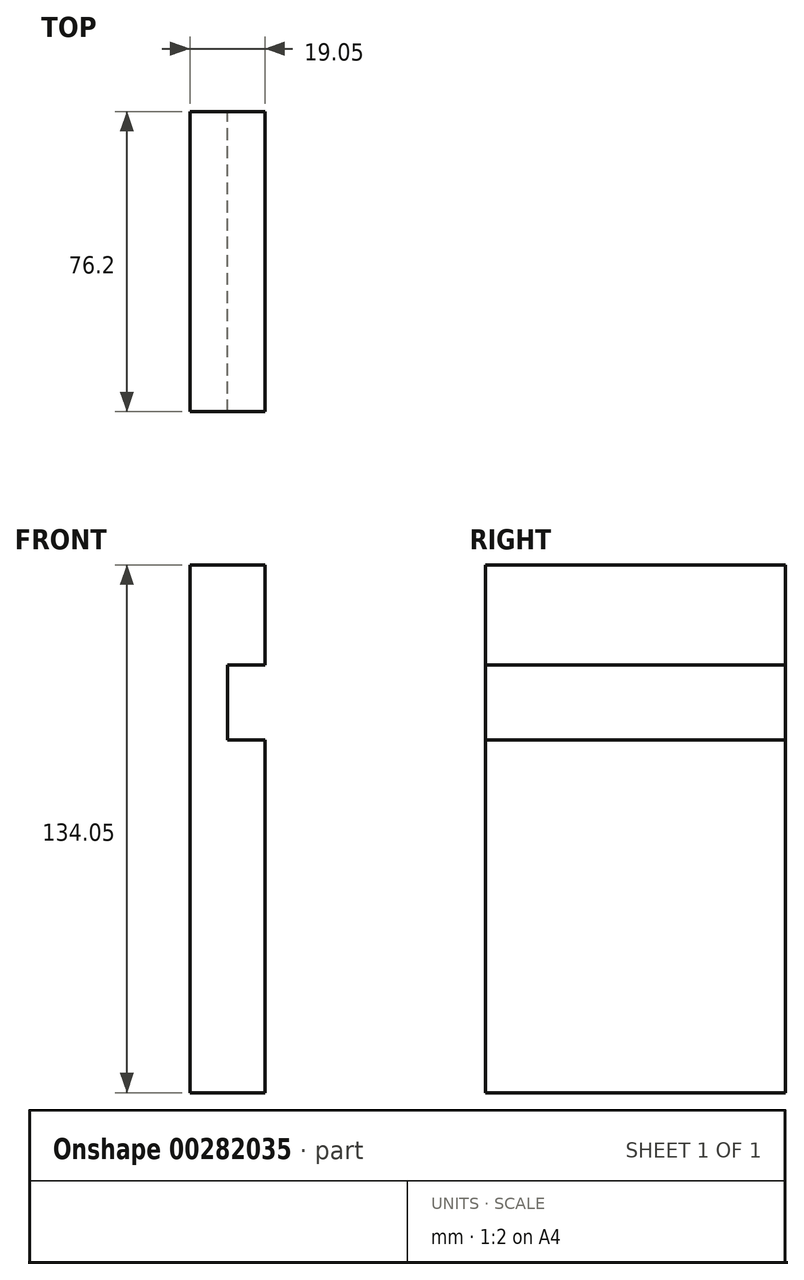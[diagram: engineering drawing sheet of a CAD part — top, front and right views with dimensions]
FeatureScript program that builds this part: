
annotation { "Feature Type Name" : "Feature", "Feature Type Description" : "" }
export const myFeature = defineFeature(function(context is Context, id is Id, definition is map)
    precondition{}
    {
        {
            var Q0;
            Q0=qCreatedBy(makeId("Front.planeOp"),FACE);
            var sketch = newSketch(context, id + "F0", { "sketchPlane" : qUnion([Q0])});
            skLineSegment(sketch, "E0", {"start": v(0, -75.8) * mm, "end": v(0, 58.24) * mm});
            skLineSegment(sketch, "E1", {"start": v(0, 58.24) * mm, "end": v(19.05, 58.24) * mm});
            skLineSegment(sketch, "E2", {"start": v(19.05, 58.24) * mm, "end": v(19.05, 32.84) * mm});
            skLineSegment(sketch, "E3", {"start": v(19.05, 32.84) * mm, "end": v(9.53, 32.84) * mm});
            skLineSegment(sketch, "E4", {"start": v(9.53, 32.84) * mm, "end": v(9.53, 13.8) * mm});
            skLineSegment(sketch, "E5", {"start": v(9.53, 13.8) * mm, "end": v(19.05, 13.8) * mm});
            skLineSegment(sketch, "E6", {"start": v(0, -75.8) * mm, "end": v(19.05, -75.8) * mm});
            skLineSegment(sketch, "E7", {"start": v(19.05, -75.8) * mm, "end": v(19.05, 13.8) * mm});
            skSolve(sketch);
        }
        {
            var Q0;
            Q0 = qSketchRegion(id + "F0", true);
            extrude(context, id + "F1", {"entities" : qUnion([Q0]), "depth" : 76.2 * mm});
        }
    });
